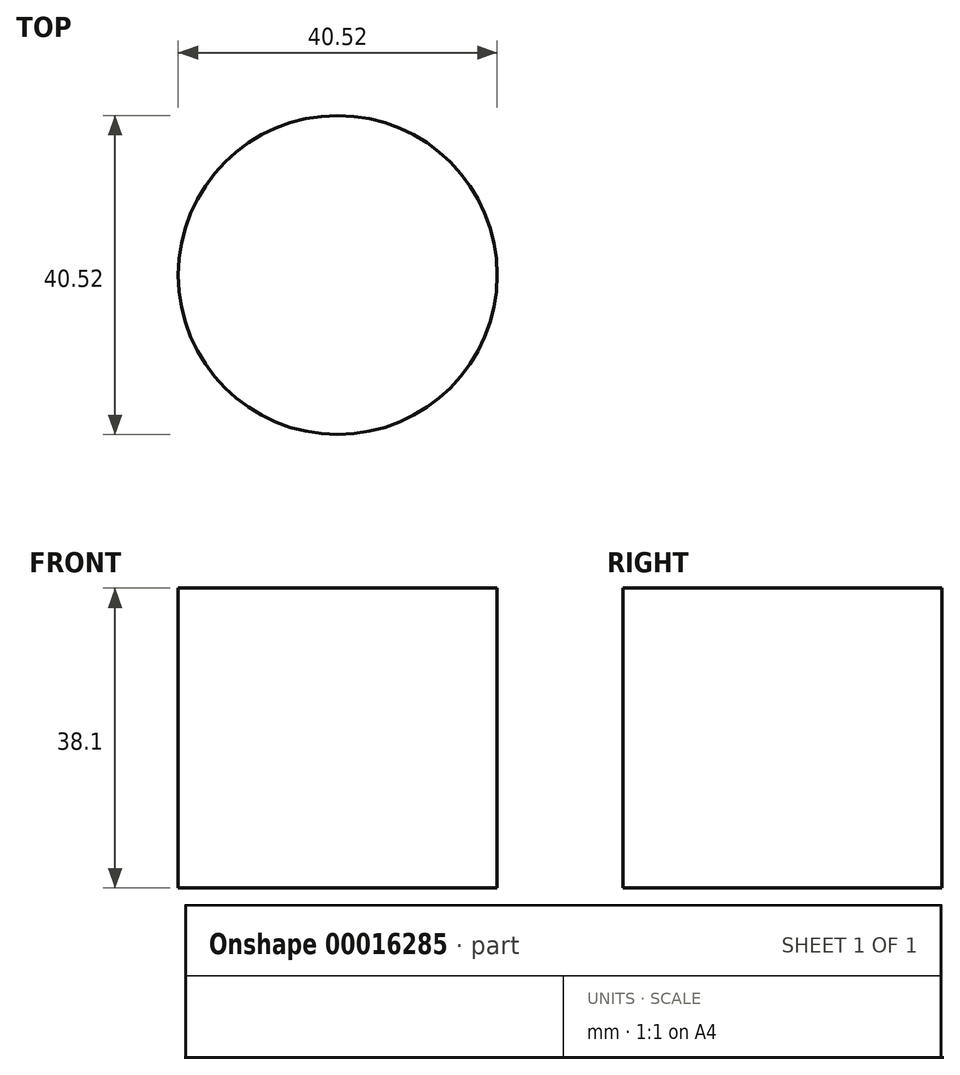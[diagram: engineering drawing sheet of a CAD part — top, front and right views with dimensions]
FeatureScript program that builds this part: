
annotation { "Feature Type Name" : "Feature", "Feature Type Description" : "" }
export const myFeature = defineFeature(function(context is Context, id is Id, definition is map)
    precondition{}
    {
        {
            var Q0;
            Q0=qCreatedBy(makeId("Front.planeOp"),FACE);
            var sketch = newSketch(context, id + "F0", { "sketchPlane" : qUnion([Q0])});
            skLineSegment(sketch, "E0.bottom", {"start": v(0, 0) * mm, "end": v(20.26, 0) * mm});
            skLineSegment(sketch, "E0.top", {"start": v(0, 38.1) * mm, "end": v(20.26, 38.1) * mm});
            skLineSegment(sketch, "E0.left", {"start": v(0, 0) * mm, "end": v(0, 38.1) * mm});
            skLineSegment(sketch, "E0.right", {"start": v(20.26, 0) * mm, "end": v(20.26, 38.1) * mm});
            skSolve(sketch);
        }
        {
            var Q0;
            Q0 = qSketchRegion(id + "F0", true);
            var Q1;
            Q1=sQuery(id+"F0.wireOp",EDGE,"E0.left");
            revolve(context, id + "F1", {"entities" : qUnion([Q0]), "axis" : qUnion([Q1]), "revolveType" : RevolveType.FULL});
        }
    });
